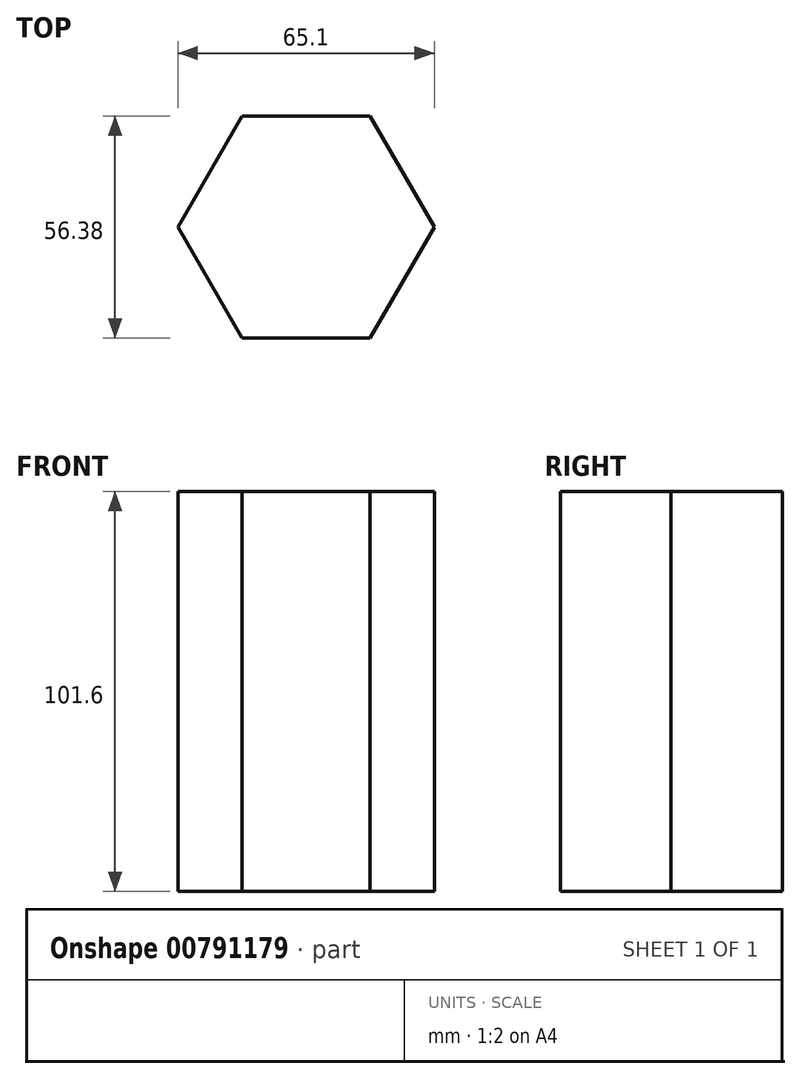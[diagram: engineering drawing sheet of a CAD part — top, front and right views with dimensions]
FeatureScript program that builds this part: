
annotation { "Feature Type Name" : "Feature", "Feature Type Description" : "" }
export const myFeature = defineFeature(function(context is Context, id is Id, definition is map)
    precondition{}
    {
        {
            var Q0;
            Q0=qCreatedBy(makeId("Top.planeOp"),FACE);
            var sketch = newSketch(context, id + "F0", { "sketchPlane" : qUnion([Q0])});
            skCircle(sketch, "E0.cCircle", {"center": v(0, 0) * mm, "radius": 32.55 * mm, "construction": true});
            skLineSegment(sketch, "E0.0", {"start": v(32.55, 0) * mm, "end": v(16.28, -28.2) * mm});
            skLineSegment(sketch, "E0.1", {"start": v(16.28, -28.2) * mm, "end": v(-16.28, -28.2) * mm});
            skLineSegment(sketch, "E0.2", {"start": v(-16.28, -28.2) * mm, "end": v(-32.55, 0) * mm});
            skLineSegment(sketch, "E0.3", {"start": v(-32.55, 0) * mm, "end": v(-16.28, 28.2) * mm});
            skLineSegment(sketch, "E0.4", {"start": v(-16.28, 28.2) * mm, "end": v(16.28, 28.2) * mm});
            skLineSegment(sketch, "E0.5", {"start": v(16.28, 28.2) * mm, "end": v(32.55, 0) * mm});
            skSolve(sketch);
        }
        {
            var Q0;
            Q0=makeQuery(id+"F0.imprint","IMPRINT",FACE,{"disambiguationData":[TD([[makeQuery(id+"F0.imprint","IMPRINT",EDGE,{"derivedFrom":sQuery(id+"F0.wireOp",EDGE,"E0.0")}),-1.0]])]});
            extrude(context, id + "F1", {"entities" : qUnion([Q0]), "depth" : 101.6 * mm, "offsetDistance" : 25.4 * mm});
        }
    });
